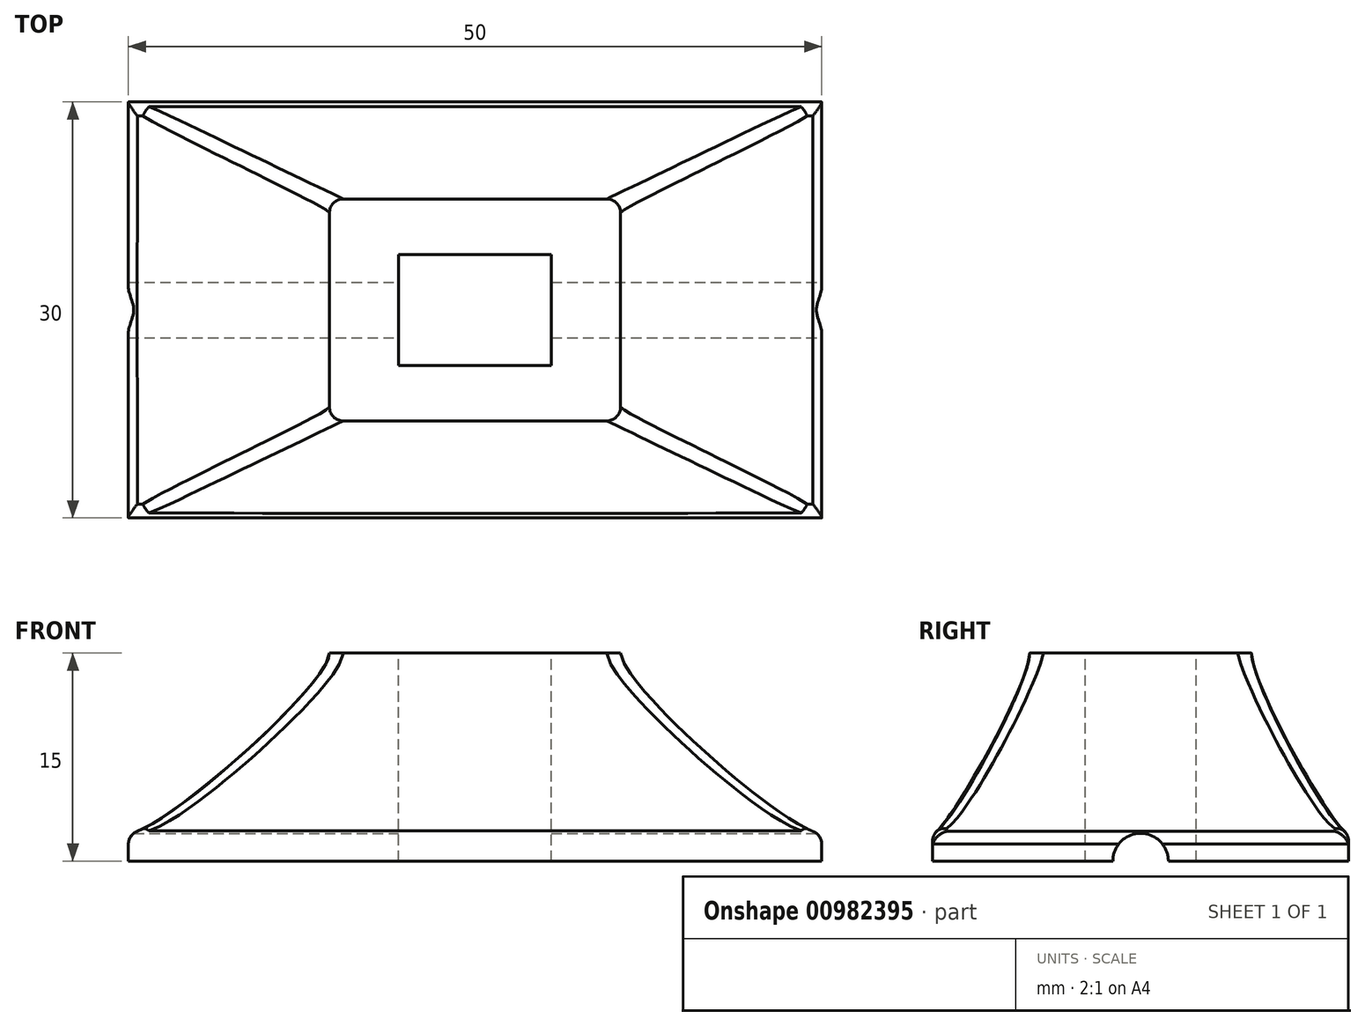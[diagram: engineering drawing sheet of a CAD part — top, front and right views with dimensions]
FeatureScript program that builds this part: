
annotation { "Feature Type Name" : "Feature", "Feature Type Description" : "" }
export const myFeature = defineFeature(function(context is Context, id is Id, definition is map)
    precondition{}
    {
        {
            var Q0;
            Q0=qCreatedBy(makeId("Top.planeOp"),FACE);
            var sketch = newSketch(context, id + "F0", { "sketchPlane" : qUnion([Q0])});
            skLineSegment(sketch, "E0.bottom", {"start": v(25, -15) * mm, "end": v(-25, -15) * mm});
            skLineSegment(sketch, "E0.top", {"start": v(25, 15) * mm, "end": v(-25, 15) * mm});
            skLineSegment(sketch, "E0.left", {"start": v(25, -15) * mm, "end": v(25, 15) * mm});
            skLineSegment(sketch, "E0.right", {"start": v(-25, -15) * mm, "end": v(-25, 15) * mm});
            skPoint(sketch, "E0.middle", {"position": v(0, 0) * mm});
            skSolve(sketch);
        }
        {
            var Q0;
            Q0=makeQuery(id+"F0.imprint","IMPRINT",FACE,{"disambiguationData":[TD([[makeQuery(id+"F0.imprint","IMPRINT",EDGE,{"derivedFrom":sQuery(id+"F0.wireOp",EDGE,"E0.bottom")}),-1.0]])]});
            cPlane(context, id + "F1", {"entities" : qUnion([Q0]), "cplaneType" : CPlaneType.OFFSET, "offset" : 13 * mm, "width" : 150 * mm, "height" : 150 * mm});
        }
        {
            var Q0;
            Q0=qCreatedBy(id+"F1.planeOp",FACE);
            var sketch = newSketch(context, id + "F2", { "sketchPlane" : qUnion([Q0])});
            skLineSegment(sketch, "E1.bottom", {"start": v(10.5, 8) * mm, "end": v(-10.5, 8) * mm});
            skLineSegment(sketch, "E1.top", {"start": v(10.5, -8) * mm, "end": v(-10.5, -8) * mm});
            skLineSegment(sketch, "E1.left", {"start": v(10.5, 8) * mm, "end": v(10.5, -8) * mm});
            skLineSegment(sketch, "E1.right", {"start": v(-10.5, 8) * mm, "end": v(-10.5, -8) * mm});
            skPoint(sketch, "E1.middle", {"position": v(0, 0) * mm});
            skSolve(sketch);
        }
        {
            var Q0;
            Q0=makeQuery(id+"F0.imprint","IMPRINT",FACE,{"disambiguationData":[TD([[makeQuery(id+"F0.imprint","IMPRINT",EDGE,{"derivedFrom":sQuery(id+"F0.wireOp",EDGE,"E0.bottom")}),-1.0]])]});
            var Q1;
            Q1=makeQuery(id+"F2.imprint","IMPRINT",FACE,{"disambiguationData":[TD([[makeQuery(id+"F2.imprint","IMPRINT",EDGE,{"derivedFrom":sQuery(id+"F2.wireOp",EDGE,"E1.bottom")}),1.0]])]});
            loft(context, id + "F3", {"startCondition" : LoftEndDerivativeType.TANGENT_TO_PROFILE, "startMagnitude" : 0.5, "endCondition" : LoftEndDerivativeType.NORMAL_TO_PROFILE, "endMagnitude" : 0.5, "sheetProfilesArray" : [{ "sheetProfileEntities" : qUnion([Q0]) }, { "sheetProfileEntities" : qUnion([Q1]) }]});
        }
        {
            var Q0;
            Q0 = qSketchRegion(id + "F0", true);
            extrude(context, id + "F4", {"entities" : qUnion([Q0]), "operationType" : NewBodyOperationType.ADD, "depth" : -2 * mm, "offsetDistance" : 25 * mm});
        }
        {
            var Q0;
            Q0=makeQuery(id+"F3.opLoft","SWEPT_EDGE",EDGE,{"disambiguationData":[OSD([sQuery(id+"F0.wireOp",EDGE,"E0.bottom"),sQuery(id+"F0.wireOp",EDGE,"E0.right"),sQuery(id+"F2.wireOp",EDGE,"E1.top"),sQuery(id+"F2.wireOp",EDGE,"E1.right")])]});
            var Q1;
            Q1=makeQuery(id+"F3.opLoft","SWEPT_EDGE",EDGE,{"disambiguationData":[OSD([sQuery(id+"F0.wireOp",EDGE,"E0.bottom"),sQuery(id+"F0.wireOp",EDGE,"E0.left"),sQuery(id+"F2.wireOp",EDGE,"E1.top"),sQuery(id+"F2.wireOp",EDGE,"E1.left")])]});
            var Q2;
            Q2=makeQuery(id+"F3.opLoft","SWEPT_EDGE",EDGE,{"disambiguationData":[OSD([sQuery(id+"F0.wireOp",EDGE,"E0.top"),sQuery(id+"F0.wireOp",EDGE,"E0.left"),sQuery(id+"F2.wireOp",EDGE,"E1.bottom"),sQuery(id+"F2.wireOp",EDGE,"E1.left")])]});
            var Q3;
            Q3=makeQuery(id+"F3.opLoft","SWEPT_EDGE",EDGE,{"disambiguationData":[OSD([sQuery(id+"F0.wireOp",EDGE,"E0.top"),sQuery(id+"F0.wireOp",EDGE,"E0.right"),sQuery(id+"F2.wireOp",EDGE,"E1.bottom"),sQuery(id+"F2.wireOp",EDGE,"E1.right")])]});
            fillet(context, id + "F5", {"entities" : qUnion([Q0, Q1, Q2, Q3]), "radius" : 1 * mm, "tangentPropagation" : true, "allowEdgeOverflow" : false});
        }
        {
            var Q0;
            {var subQ0=sQuery(id+"F0.wireOp",EDGE,"E0.left");Q0=makeQuery(id+"F4.boolean.opBoolean","MERGE",EDGE,{"derivedFrom":[makeQuery(id+"F3.opLoft","MID_CAP_EDGE",EDGE,{"disambiguationData":[OSD([sQuery(id+"F0.wireOp",EDGE,"E0.bottom"),sQuery(id+"F0.wireOp",EDGE,"E0.top"),subQ0])],"capPos":0.0}),makeQuery(id+"F4.opExtrude","CAP_EDGE",EDGE,{"disambiguationData":[OSD([subQ0])],"isStart":true})]});}
            var Q1;
            {var subQ0=sQuery(id+"F0.wireOp",EDGE,"E0.bottom");Q1=makeQuery(id+"F4.boolean.opBoolean","MERGE",EDGE,{"derivedFrom":[makeQuery(id+"F3.opLoft","MID_CAP_EDGE",EDGE,{"disambiguationData":[OSD([subQ0,sQuery(id+"F0.wireOp",EDGE,"E0.left"),sQuery(id+"F0.wireOp",EDGE,"E0.right")])],"capPos":0.0}),makeQuery(id+"F4.opExtrude","CAP_EDGE",EDGE,{"disambiguationData":[OSD([subQ0])],"isStart":true})]});}
            var Q2;
            {var subQ0=sQuery(id+"F0.wireOp",EDGE,"E0.right");Q2=makeQuery(id+"F4.boolean.opBoolean","MERGE",EDGE,{"derivedFrom":[makeQuery(id+"F3.opLoft","MID_CAP_EDGE",EDGE,{"disambiguationData":[OSD([sQuery(id+"F0.wireOp",EDGE,"E0.bottom"),sQuery(id+"F0.wireOp",EDGE,"E0.top"),subQ0])],"capPos":0.0}),makeQuery(id+"F4.opExtrude","CAP_EDGE",EDGE,{"disambiguationData":[OSD([subQ0])],"isStart":true})]});}
            var Q3;
            {var subQ0=sQuery(id+"F0.wireOp",EDGE,"E0.top");Q3=makeQuery(id+"F4.boolean.opBoolean","MERGE",EDGE,{"derivedFrom":[makeQuery(id+"F3.opLoft","MID_CAP_EDGE",EDGE,{"disambiguationData":[OSD([subQ0,sQuery(id+"F0.wireOp",EDGE,"E0.left"),sQuery(id+"F0.wireOp",EDGE,"E0.right")])],"capPos":0.0}),makeQuery(id+"F4.opExtrude","CAP_EDGE",EDGE,{"disambiguationData":[OSD([subQ0])],"isStart":true})]});}
            fillet(context, id + "F6", {"entities" : qUnion([Q0, Q1, Q2, Q3]), "radius" : 1 * mm, "tangentPropagation" : true, "allowEdgeOverflow" : false});
        }
        {
            var Q0;
            Q0=qCreatedBy(id+"F1.planeOp",FACE);
            var sketch = newSketch(context, id + "F7", { "sketchPlane" : qUnion([Q0])});
            skLineSegment(sketch, "E2.bottom", {"start": v(-5.5, 4) * mm, "end": v(5.5, 4) * mm});
            skLineSegment(sketch, "E2.top", {"start": v(-5.5, -4) * mm, "end": v(5.5, -4) * mm});
            skLineSegment(sketch, "E2.left", {"start": v(-5.5, 4) * mm, "end": v(-5.5, -4) * mm});
            skLineSegment(sketch, "E2.right", {"start": v(5.5, 4) * mm, "end": v(5.5, -4) * mm});
            skPoint(sketch, "E2.middle", {"position": v(0, 0) * mm});
            skSolve(sketch);
        }
        {
            var Q0;
            Q0=makeQuery(id+"F7.imprint","IMPRINT",FACE,{"disambiguationData":[TD([[makeQuery(id+"F7.imprint","IMPRINT",EDGE,{"derivedFrom":sQuery(id+"F7.wireOp",EDGE,"E2.bottom")}),-1.0]])]});
            extrude(context, id + "F8", {"entities" : qUnion([Q0]), "operationType" : NewBodyOperationType.REMOVE, "oppositeDirection" : true, "depth" : 25 * mm, "offsetDistance" : 25 * mm});
        }
        {
            var Q0;
            Q0=makeQuery(id+"F4.opExtrude","SWEPT_FACE",FACE,{"disambiguationData":[OSD([sQuery(id+"F0.wireOp",EDGE,"E0.left")])]});
            var sketch = newSketch(context, id + "F9", { "sketchPlane" : qUnion([Q0])});
            skCircle(sketch, "E3", {"center": v(0, -2) * mm, "radius": 2 * mm});
            skSolve(sketch);
        }
        {
            var Q0;
            {var subQ0=sQuery(id+"F9.wireOp",EDGE,"E3");var subQ1=sQuery(id+"F0.wireOp",EDGE,"E0.left");var subQ4=makeQuery(id+"F4.opExtrude","CAP_EDGE",EDGE,{"disambiguationData":[OSD([subQ1])],"isStart":false});var subQ5=makeQuery(id+"F9.imprint","INTERSECT",VERTEX,{"disambiguationData":[OD(0.0)],"derivedFrom":[subQ4,subQ0]});Q0=makeQuery(id+"F9.imprint","IMPRINT",FACE,{"disambiguationData":[TD([[makeQuery(id+"F9.imprint","IMPRINT",EDGE,{"disambiguationData":[TD([[subQ5,1.0]])],"derivedFrom":subQ4}),1.0]])]});}
            var Q1;
            {var subQ0=sQuery(id+"F9.wireOp",EDGE,"E3");var subQ1=sQuery(id+"F0.wireOp",EDGE,"E0.left");var subQ2=makeQuery(id+"F6.opFillet","BLEND_EDGE",EDGE,{"blendedFrom":[makeQuery(id+"F4.boolean.opBoolean","MERGE",EDGE,{"derivedFrom":[makeQuery(id+"F3.opLoft","MID_CAP_EDGE",EDGE,{"disambiguationData":[OSD([sQuery(id+"F0.wireOp",EDGE,"E0.bottom"),sQuery(id+"F0.wireOp",EDGE,"E0.top"),subQ1])],"capPos":0.0}),makeQuery(id+"F4.opExtrude","CAP_EDGE",EDGE,{"disambiguationData":[OSD([subQ1])],"isStart":true})]}),makeQuery(id+"F4.opExtrude","SWEPT_FACE",FACE,{"disambiguationData":[OSD([subQ1])]})],"blendedInto":[makeQuery(id+"F4.opExtrude","SWEPT_FACE",FACE,{"disambiguationData":[OSD([subQ1])]})]});var subQ3=makeQuery(id+"F9.imprint","INTERSECT",VERTEX,{"disambiguationData":[OD(0.0)],"derivedFrom":[subQ2,subQ0]});Q1=makeQuery(id+"F9.imprint","IMPRINT",FACE,{"disambiguationData":[TD([[makeQuery(id+"F9.imprint","IMPRINT",EDGE,{"disambiguationData":[TD([[subQ3,-1.0]])],"derivedFrom":subQ0}),1.0]])]});}
            var Q2;
            Q2=sQuery(id+"F9.wireOp",EDGE,"E3");
            extrude(context, id + "F10", {"entities" : qUnion([Q0, Q1]), "operationType" : NewBodyOperationType.REMOVE, "surfaceEntities" : qUnion([Q2]), "endBound" : BoundingType.THROUGH_ALL, "oppositeDirection" : true, "depth" : 25 * mm, "offsetDistance" : 25 * mm});
        }
    });
